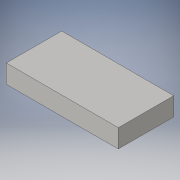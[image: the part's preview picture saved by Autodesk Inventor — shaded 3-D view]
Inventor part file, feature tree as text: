
AUTODESK INVENTOR PART (.ipt)
format: ipt  version: 2016 (Build 200138000, 138)  size: 83,968 bytes
history: native  units: in
note: dims shown in document units (in); Inventor stores cm internally (conversion verified against a paired STEP export)
features: extrude x1, sketch x1
ambient origin geometry x8: Origin, YZ Plane, XZ Plane, XY Plane, X Axis, Y Axis, Z Axis, Center Point
bodies: Solid1 (feature_tree)
feature tree (2):
  extrude  "Extrusion1"  Depth=3.0in
  sketch  "Sketch1"  dims[d0=6.07in d1=3.0in d2=1.0in d3=0.0in]
